# Revit family: MPS
name_source: partatom
category: Lighting Fixtures
units: mm (PartAtom-declared; Revit-internal decimal feet)

## family parameters
Cut with Voids When Loaded = No
Host = Face
Light Source = Yes
OmniClass Number = 23.80.70.11.14.17
OmniClass Title = Direct/Indirect
Part Type = Normal
Room Calculation Point = No
Round Connector Dimension = Use Diameter
Shared = Yes

## types (3) — shared parameters
Apparent Load = 14 VA
Assembly Code = D5020200
Ceiling Type = Surface mount, wall mount or suspended
Color Filter = 16777215
Default Elevation = 48"
Description = MultiPurpose Linear
Dimming Lamp Color Temperature Shift = Incandescent Lamp Curve
Emit Shape Visible in Rendering = No
Emit from Rectangle Width = 3"
Finish = Arctic White
Glass = White Glass
Lamp = LED
Lens Option = Curve Lens
Load Classification = Lighting
Manufacturer = Columbia Lighting
Model = MPS
Photometric Notes = More IES files download in Photometric Web Link
Photometric Web File = MPS2-30HL-CN-EDU.ies
Power Factor = 1
Tilt Angle = 90.00°
Type Comments = Lighting Fixture
URL = https://www.currentlighting.com
Voltage = 120 V
Warranty = Five year warranty
Wattage Comments = 13.8W to 133.0
Watts = 14 W

## per-type parameters (varying)
| type | Emit from Rectangle Length | zz Length 2 |
| MPS-4 | 46" | 48" |
| MPS-2 | 22" | 24" |
| MPS-8 | 94" | 96" |

## geometry (parser evidence)
native form markers: Blend x2, Sweep x7
no freeform markers — native parametric forms only
